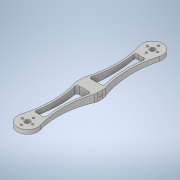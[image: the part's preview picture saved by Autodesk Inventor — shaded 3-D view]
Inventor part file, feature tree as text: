
AUTODESK INVENTOR PART (.ipt)
format: ipt  version: 2020 (Build 240168000, 168)  size: 443,904 bytes
history: native  units: in
note: dims shown in document units (in); Inventor stores cm internally (conversion verified against a paired STEP export)
features: extrude x7, sketch x7, fillet x5, plane x2, mirror x1
ambient origin geometry x8: Origin, YZ Plane, XZ Plane, XY Plane, X Axis, Y Axis, Z Axis, Center Point
bodies: Solid1 (feature_tree)
feature tree (22):
  extrude  "Extrusion1"  Depth=4.5in
  fillet  "Fillet1"  Radius=4.5in
  extrude  "Extrusion2"  Depth=0.135in
  extrude  "Extrusion3"  Depth=0.625in
  extrude  "Extrusion4"  Depth=1.25in
  fillet  "Fillet2"  Radius=0.5in
  mirror  "Mirror1"
  extrude  "Extrusion5"  Depth=6.0in
  plane  "Work Plane1"
  extrude  "Extrusion6"  Depth=1.25in
  fillet  "Fillet3"  Radius=9.0in
  fillet  "Fillet4"  Radius=1.0in
  fillet  "Fillet5"  Radius=0.625in
  plane  "Work Plane2"
  extrude  "Extrusion7"  Depth=0.125in
  sketch  "Sketch1"  dims[d0=0.5in d1=4.5in d2=4.5in]
  sketch  "Sketch2"  dims[d3=0.25in d4=0.135in]
  sketch  "Sketch3"  dims[d5=1.25in d6=0.0in d7=0.625in]
  sketch  "Sketch4"  dims[d8=4.5in d9=1.25in d10=0.5in]
  sketch  "Sketch5"  dims[d11=6.0in d12=6.0in]
  sketch  "Sketch8"  dims[d13=0.8125in d14=0.0in d15=1.25in d16=9.0in d17=1.0in d18=0.0in d19=0.625in]
  sketch  "Sketch9"  dims[d20=6.0in d21=6.0in d22=1.25in d23=1.5in d24=12.25in d25=12.25in d26=0.125in d27=1.0in d28=0.0in d29=0.625in d30=0.748in d31=0.6299in d32=0.748in d33=0.6299in d34=0.125in d35=0.125in d36=0.125in d37=0.125in d38=0.125in d39=0.125in d40=0.125in d41=0.125in d42=0.25in d43=0.25in d44=1.0in d45=0.0in d46=-0.1969in d47=0.2362in d48=0.2362in d49=0.2362in d50=0.2362in d51=0.2362in d52=0.2362in d53=0.2362in d54=0.2362in d55=1.0in d56=0.0in d57=0.0394in d58=0.0394in d59=0.125in d60=-0.25in d61=1.0in d62=0.0in d63=1.2848in]
